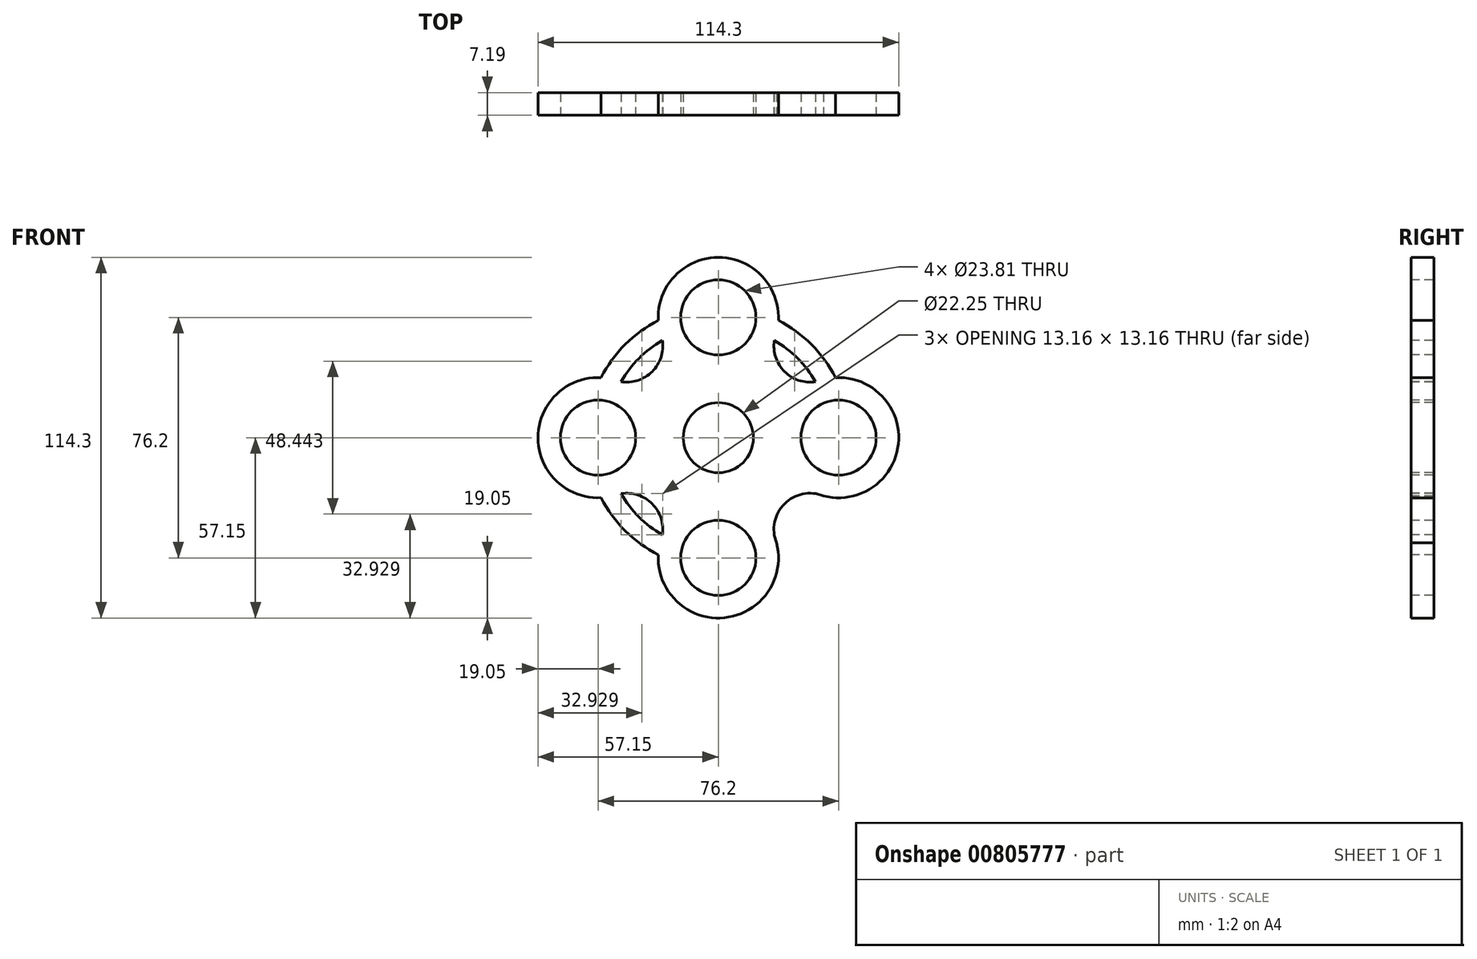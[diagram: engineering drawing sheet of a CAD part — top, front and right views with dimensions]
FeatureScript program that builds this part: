
annotation { "Feature Type Name" : "Feature", "Feature Type Description" : "" }
export const myFeature = defineFeature(function(context is Context, id is Id, definition is map)
    precondition{}
    {
        {
            var Q0;
            Q0=qCreatedBy(makeId("Front.planeOp"),FACE);
            var sketch = newSketch(context, id + "F0", { "sketchPlane" : qUnion([Q0])});
            skCircle(sketch, "E0", {"center": v(0, 0) * mm, "radius": 38.1 * mm});
            skSolve(sketch);
        }
        {
            var Q0;
            Q0=makeQuery(id+"F0.imprint","IMPRINT",FACE,{"disambiguationData":[TD([[makeQuery(id+"F0.imprint","IMPRINT",EDGE,{"derivedFrom":sQuery(id+"F0.wireOp",EDGE,"E0")}),1.0]])]});
            extrude(context, id + "F1", {"entities" : qUnion([Q0]), "depth" : 7.2 * mm, "offsetDistance" : 25.4 * mm});
        }
        {
            var Q0;
            Q0=makeQuery(id+"F1.opExtrude","CAP_FACE",FACE,{"disambiguationData":[OSD([sQuery(id+"F0.wireOp",EDGE,"E0")])],"isStart":false});
            var sketch = newSketch(context, id + "F2", { "sketchPlane" : qUnion([Q0])});
            skCircle(sketch, "E1", {"center": v(0, 0) * mm, "radius": 11.13 * mm});
            skSolve(sketch);
        }
        {
            var Q0;
            Q0=makeQuery(id+"F2.imprint","IMPRINT",FACE,{"disambiguationData":[TD([[makeQuery(id+"F2.imprint","IMPRINT",EDGE,{"derivedFrom":sQuery(id+"F2.wireOp",EDGE,"E1")}),1.0]])]});
            extrude(context, id + "F3", {"entities" : qUnion([Q0]), "operationType" : NewBodyOperationType.REMOVE, "oppositeDirection" : true, "depth" : 7.62 * mm, "offsetDistance" : 25.4 * mm});
        }
        {
            var Q0;
            Q0=makeQuery(id+"F1.opExtrude","CAP_FACE",FACE,{"disambiguationData":[OSD([sQuery(id+"F0.wireOp",EDGE,"E0")])],"isStart":false});
            var sketch = newSketch(context, id + "F4", { "sketchPlane" : qUnion([Q0])});
            skCircle(sketch, "E2", {"center": v(38.1, 0) * mm, "radius": 19.05 * mm});
            skCircle(sketch, "E3", {"center": v(0, -38.1) * mm, "radius": 19.05 * mm});
            skCircle(sketch, "E4", {"center": v(-38.1, 0) * mm, "radius": 19.05 * mm});
            skCircle(sketch, "E5", {"center": v(0, 38.1) * mm, "radius": 19.05 * mm});
            skSolve(sketch);
        }
        {
            var Q0;
            {var subQ0=sQuery(id+"F4.wireOp",EDGE,"E5");var subQ1=makeQuery(id+"F1.opExtrude","CAP_EDGE",EDGE,{"disambiguationData":[OSD([sQuery(id+"F0.wireOp",EDGE,"E0")])],"isStart":false});var subQ2=makeQuery(id+"F4.imprint","INTERSECT",VERTEX,{"disambiguationData":[OD(0.0)],"derivedFrom":[subQ1,subQ0]});Q0=makeQuery(id+"F4.imprint","IMPRINT",FACE,{"disambiguationData":[TD([[makeQuery(id+"F4.imprint","IMPRINT",EDGE,{"disambiguationData":[TD([[subQ2,1.0]])],"derivedFrom":subQ0}),1.0]])]});}
            var Q1;
            {var subQ0=sQuery(id+"F4.wireOp",EDGE,"E4");var subQ1=makeQuery(id+"F1.opExtrude","CAP_EDGE",EDGE,{"disambiguationData":[OSD([sQuery(id+"F0.wireOp",EDGE,"E0")])],"isStart":false});var subQ2=makeQuery(id+"F4.imprint","INTERSECT",VERTEX,{"disambiguationData":[OD(0.0)],"derivedFrom":[subQ1,subQ0]});Q1=makeQuery(id+"F4.imprint","IMPRINT",FACE,{"disambiguationData":[TD([[makeQuery(id+"F4.imprint","IMPRINT",EDGE,{"disambiguationData":[TD([[subQ2,1.0]])],"derivedFrom":subQ0}),1.0]])]});}
            var Q2;
            {var subQ0=sQuery(id+"F4.wireOp",EDGE,"E3");var subQ1=makeQuery(id+"F1.opExtrude","CAP_EDGE",EDGE,{"disambiguationData":[OSD([sQuery(id+"F0.wireOp",EDGE,"E0")])],"isStart":false});var subQ2=makeQuery(id+"F4.imprint","INTERSECT",VERTEX,{"disambiguationData":[OD(0.0)],"derivedFrom":[subQ1,subQ0]});Q2=makeQuery(id+"F4.imprint","IMPRINT",FACE,{"disambiguationData":[TD([[makeQuery(id+"F4.imprint","IMPRINT",EDGE,{"disambiguationData":[TD([[subQ2,-1.0]])],"derivedFrom":subQ0}),1.0]])]});}
            var Q3;
            {var subQ0=sQuery(id+"F4.wireOp",EDGE,"E2");var subQ1=makeQuery(id+"F1.opExtrude","CAP_EDGE",EDGE,{"disambiguationData":[OSD([sQuery(id+"F0.wireOp",EDGE,"E0")])],"isStart":false});var subQ2=makeQuery(id+"F4.imprint","INTERSECT",VERTEX,{"disambiguationData":[OD(0.0)],"derivedFrom":[subQ1,subQ0]});Q3=makeQuery(id+"F4.imprint","IMPRINT",FACE,{"disambiguationData":[TD([[makeQuery(id+"F4.imprint","IMPRINT",EDGE,{"disambiguationData":[TD([[subQ2,-1.0]])],"derivedFrom":subQ0}),1.0]])]});}
            extrude(context, id + "F5", {"entities" : qUnion([Q0, Q1, Q2, Q3]), "operationType" : NewBodyOperationType.ADD, "oppositeDirection" : true, "depth" : 7.2 * mm, "offsetDistance" : 25.4 * mm});
        }
        {
            var Q0;
            {var subQ0=sQuery(id+"F0.wireOp",EDGE,"E0");Q0=makeQuery(id+"F5.boolean.opBoolean","MERGE",FACE,{"derivedFrom":[makeQuery(id+"F1.opExtrude","CAP_FACE",FACE,{"disambiguationData":[OSD([subQ0])],"isStart":false}),makeQuery(id+"F5.opExtrude","CAP_FACE",FACE,{"disambiguationData":[OSD([subQ0,sQuery(id+"F4.wireOp",EDGE,"E2")])],"isStart":true}),makeQuery(id+"F5.opExtrude","CAP_FACE",FACE,{"disambiguationData":[OSD([subQ0,sQuery(id+"F4.wireOp",EDGE,"E3")])],"isStart":true}),makeQuery(id+"F5.opExtrude","CAP_FACE",FACE,{"disambiguationData":[OSD([subQ0,sQuery(id+"F4.wireOp",EDGE,"E4")])],"isStart":true}),makeQuery(id+"F5.opExtrude","CAP_FACE",FACE,{"disambiguationData":[OSD([subQ0,sQuery(id+"F4.wireOp",EDGE,"E5")])],"isStart":true})]});}
            var sketch = newSketch(context, id + "F6", { "sketchPlane" : qUnion([Q0])});
            skArc(sketch, "E6", {"start": v(18.45, 33.34) * mm, "mid": v(20.95, 20.95) * mm, "end": v(33.34, 18.45) * mm});
            skArc(sketch, "E7", {"start": v(-33.34, 18.45) * mm, "mid": v(-20.95, 20.95) * mm, "end": v(-18.45, 33.34) * mm});
            skArc(sketch, "E8", {"start": v(-18.45, -33.34) * mm, "mid": v(-20.95, -20.95) * mm, "end": v(-33.34, -18.45) * mm});
            skArc(sketch, "E9", {"start": v(33.34, -18.45) * mm, "mid": v(20.95, -20.95) * mm, "end": v(18.45, -33.34) * mm});
            skSolve(sketch);
        }
        {
            var Q0;
            Q0=makeQuery(id+"F6.imprint","IMPRINT",FACE,{"disambiguationData":[TD([[makeQuery(id+"F6.imprint","IMPRINT",EDGE,{"derivedFrom":sQuery(id+"F6.wireOp",EDGE,"E7")}),1.0]])]});
            var Q1;
            Q1=makeQuery(id+"F6.imprint","IMPRINT",FACE,{"disambiguationData":[TD([[makeQuery(id+"F6.imprint","IMPRINT",EDGE,{"derivedFrom":sQuery(id+"F6.wireOp",EDGE,"E8")}),1.0]])]});
            var Q2;
            Q2=makeQuery(id+"F6.imprint","IMPRINT",FACE,{"disambiguationData":[TD([[makeQuery(id+"F6.imprint","IMPRINT",EDGE,{"derivedFrom":sQuery(id+"F6.wireOp",EDGE,"E9")}),1.0]])]});
            var Q3;
            Q3=makeQuery(id+"F6.imprint","IMPRINT",FACE,{"disambiguationData":[TD([[makeQuery(id+"F6.imprint","IMPRINT",EDGE,{"derivedFrom":sQuery(id+"F6.wireOp",EDGE,"E6")}),1.0]])]});
            extrude(context, id + "F7", {"entities" : qUnion([Q0, Q1, Q2, Q3]), "operationType" : NewBodyOperationType.REMOVE, "oppositeDirection" : true, "depth" : 25.4 * mm, "offsetDistance" : 25.4 * mm});
        }
        {
            var Q0;
            {var subQ0=sQuery(id+"F0.wireOp",EDGE,"E0");Q0=makeQuery(id+"F5.boolean.opBoolean","MERGE",FACE,{"derivedFrom":[makeQuery(id+"F1.opExtrude","CAP_FACE",FACE,{"disambiguationData":[OSD([subQ0])],"isStart":false}),makeQuery(id+"F5.opExtrude","CAP_FACE",FACE,{"disambiguationData":[OSD([subQ0,sQuery(id+"F4.wireOp",EDGE,"E2")])],"isStart":true}),makeQuery(id+"F5.opExtrude","CAP_FACE",FACE,{"disambiguationData":[OSD([subQ0,sQuery(id+"F4.wireOp",EDGE,"E3")])],"isStart":true}),makeQuery(id+"F5.opExtrude","CAP_FACE",FACE,{"disambiguationData":[OSD([subQ0,sQuery(id+"F4.wireOp",EDGE,"E4")])],"isStart":true}),makeQuery(id+"F5.opExtrude","CAP_FACE",FACE,{"disambiguationData":[OSD([subQ0,sQuery(id+"F4.wireOp",EDGE,"E5")])],"isStart":true})]});}
            var sketch = newSketch(context, id + "F8", { "sketchPlane" : qUnion([Q0])});
            skCircle(sketch, "E10", {"center": v(0, 0) * mm, "radius": 41.73 * mm});
            skCircle(sketch, "E11", {"center": v(0, 0) * mm, "radius": 35.55 * mm});
            skSolve(sketch);
        }
        {
            var Q0;
            {var subQ1=makeQuery(id+"F5.opExtrude","CAP_EDGE",EDGE,{"disambiguationData":[OSD([sQuery(id+"F4.wireOp",EDGE,"E4")])],"isStart":true});var subQ3=sQuery(id+"F8.wireOp",EDGE,"E10");var subQ4=makeQuery(id+"F8.imprint","INTERSECT",VERTEX,{"disambiguationData":[OD(1.0)],"derivedFrom":[subQ1,subQ3]});Q0=makeQuery(id+"F8.imprint","IMPRINT",FACE,{"disambiguationData":[TD([[makeQuery(id+"F8.imprint","IMPRINT",EDGE,{"disambiguationData":[TD([[subQ4,-1.0]])],"derivedFrom":subQ3}),1.0]])]});}
            var Q1;
            {var subQ3=sQuery(id+"F8.wireOp",EDGE,"E10");var subQ5=makeQuery(id+"F5.opExtrude","CAP_EDGE",EDGE,{"disambiguationData":[OSD([sQuery(id+"F4.wireOp",EDGE,"E3")])],"isStart":true});var subQ6=makeQuery(id+"F8.imprint","INTERSECT",VERTEX,{"disambiguationData":[OD(1.0)],"derivedFrom":[subQ5,subQ3]});Q1=makeQuery(id+"F8.imprint","IMPRINT",FACE,{"disambiguationData":[TD([[makeQuery(id+"F8.imprint","IMPRINT",EDGE,{"disambiguationData":[TD([[subQ6,-1.0]])],"derivedFrom":subQ3}),1.0]])]});}
            var Q2;
            {var subQ1=makeQuery(id+"F5.opExtrude","CAP_EDGE",EDGE,{"disambiguationData":[OSD([sQuery(id+"F4.wireOp",EDGE,"E5")])],"isStart":true});var subQ3=sQuery(id+"F8.wireOp",EDGE,"E10");var subQ4=makeQuery(id+"F8.imprint","INTERSECT",VERTEX,{"disambiguationData":[OD(0.0)],"derivedFrom":[subQ1,subQ3]});Q2=makeQuery(id+"F8.imprint","IMPRINT",FACE,{"disambiguationData":[TD([[makeQuery(id+"F8.imprint","IMPRINT",EDGE,{"disambiguationData":[TD([[subQ4,1.0]])],"derivedFrom":subQ3}),1.0]])]});}
            var Q3;
            {var subQ1=makeQuery(id+"F5.opExtrude","CAP_EDGE",EDGE,{"disambiguationData":[OSD([sQuery(id+"F4.wireOp",EDGE,"E5")])],"isStart":true});var subQ3=sQuery(id+"F8.wireOp",EDGE,"E10");var subQ4=makeQuery(id+"F8.imprint","INTERSECT",VERTEX,{"disambiguationData":[OD(1.0)],"derivedFrom":[subQ1,subQ3]});Q3=makeQuery(id+"F8.imprint","IMPRINT",FACE,{"disambiguationData":[TD([[makeQuery(id+"F8.imprint","IMPRINT",EDGE,{"disambiguationData":[TD([[subQ4,-1.0]])],"derivedFrom":subQ3}),1.0]])]});}
            extrude(context, id + "F9", {"entities" : qUnion([Q0, Q1, Q2, Q3]), "operationType" : NewBodyOperationType.ADD, "oppositeDirection" : true, "depth" : 7.2 * mm, "offsetDistance" : 25.4 * mm});
        }
        {
            var Q0;
            {var subQ0=sQuery(id+"F8.wireOp",EDGE,"E11");var subQ1=sQuery(id+"F8.wireOp",EDGE,"E10");var subQ2=sQuery(id+"F4.wireOp",EDGE,"E3");var subQ3=sQuery(id+"F4.wireOp",EDGE,"E2");var subQ4=sQuery(id+"F4.wireOp",EDGE,"E4");var subQ5=sQuery(id+"F4.wireOp",EDGE,"E5");var subQ6=sQuery(id+"F0.wireOp",EDGE,"E0");Q0=makeQuery(id+"F9.boolean.opBoolean","MERGE",FACE,{"derivedFrom":[makeQuery(id+"F5.boolean.opBoolean","MERGE",FACE,{"derivedFrom":[makeQuery(id+"F1.opExtrude","CAP_FACE",FACE,{"disambiguationData":[OSD([subQ6])],"isStart":false}),makeQuery(id+"F5.opExtrude","CAP_FACE",FACE,{"disambiguationData":[OSD([subQ6,subQ3])],"isStart":true}),makeQuery(id+"F5.opExtrude","CAP_FACE",FACE,{"disambiguationData":[OSD([subQ6,subQ2])],"isStart":true}),makeQuery(id+"F5.opExtrude","CAP_FACE",FACE,{"disambiguationData":[OSD([subQ6,subQ4])],"isStart":true}),makeQuery(id+"F5.opExtrude","CAP_FACE",FACE,{"disambiguationData":[OSD([subQ6,subQ5])],"isStart":true})]}),makeQuery(id+"F9.opExtrude","CAP_FACE",FACE,{"disambiguationData":[OSD([subQ3,subQ5,sQuery(id+"F6.wireOp",EDGE,"E6"),subQ1,subQ0])],"isStart":true}),makeQuery(id+"F9.opExtrude","CAP_FACE",FACE,{"disambiguationData":[OSD([subQ4,subQ5,sQuery(id+"F6.wireOp",EDGE,"E7"),subQ1,subQ0])],"isStart":true}),makeQuery(id+"F9.opExtrude","CAP_FACE",FACE,{"disambiguationData":[OSD([subQ2,subQ4,sQuery(id+"F6.wireOp",EDGE,"E8"),subQ1,subQ0])],"isStart":true}),makeQuery(id+"F9.opExtrude","CAP_FACE",FACE,{"disambiguationData":[OSD([subQ3,subQ2,sQuery(id+"F6.wireOp",EDGE,"E9"),subQ1,subQ0])],"isStart":true})]});}
            var sketch = newSketch(context, id + "F10", { "sketchPlane" : qUnion([Q0])});
            skCircle(sketch, "E12", {"center": v(0, 38.1) * mm, "radius": 11.9 * mm});
            skCircle(sketch, "E13", {"center": v(38.1, 0) * mm, "radius": 11.9 * mm});
            skCircle(sketch, "E14", {"center": v(0, -38.1) * mm, "radius": 11.9 * mm});
            skCircle(sketch, "E15", {"center": v(-38.1, 0) * mm, "radius": 11.9 * mm});
            skSolve(sketch);
        }
        {
            var Q0;
            Q0=makeQuery(id+"F10.imprint","IMPRINT",FACE,{"disambiguationData":[TD([[makeQuery(id+"F10.imprint","IMPRINT",EDGE,{"derivedFrom":sQuery(id+"F10.wireOp",EDGE,"E15")}),1.0]])]});
            var Q1;
            Q1=makeQuery(id+"F10.imprint","IMPRINT",FACE,{"disambiguationData":[TD([[makeQuery(id+"F10.imprint","IMPRINT",EDGE,{"derivedFrom":sQuery(id+"F10.wireOp",EDGE,"E12")}),1.0]])]});
            var Q2;
            Q2=makeQuery(id+"F10.imprint","IMPRINT",FACE,{"disambiguationData":[TD([[makeQuery(id+"F10.imprint","IMPRINT",EDGE,{"derivedFrom":sQuery(id+"F10.wireOp",EDGE,"E13")}),1.0]])]});
            var Q3;
            Q3=makeQuery(id+"F10.imprint","IMPRINT",FACE,{"disambiguationData":[TD([[makeQuery(id+"F10.imprint","IMPRINT",EDGE,{"derivedFrom":sQuery(id+"F10.wireOp",EDGE,"E14")}),1.0]])]});
            extrude(context, id + "F11", {"entities" : qUnion([Q0, Q1, Q2, Q3]), "operationType" : NewBodyOperationType.REMOVE, "oppositeDirection" : true, "depth" : 25.4 * mm, "offsetDistance" : 25.4 * mm});
        }
    });
